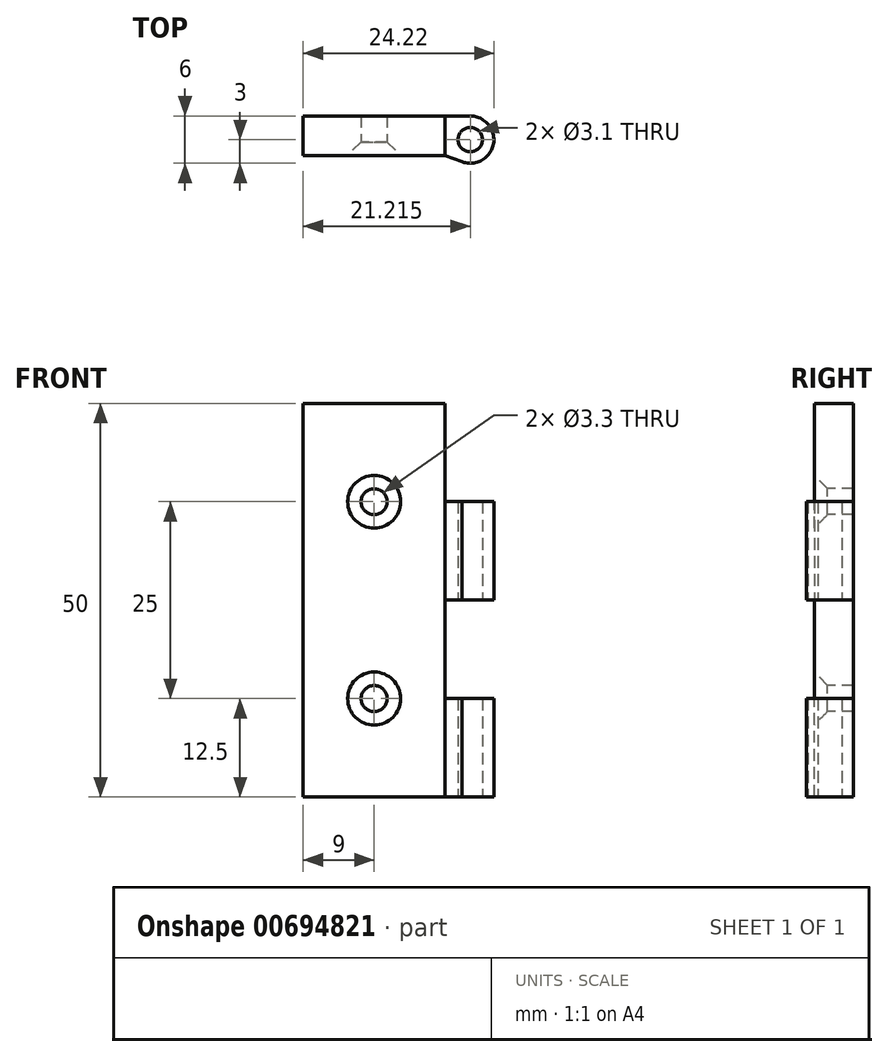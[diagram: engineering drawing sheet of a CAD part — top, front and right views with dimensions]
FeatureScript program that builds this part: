
annotation { "Feature Type Name" : "Feature", "Feature Type Description" : "" }
export const myFeature = defineFeature(function(context is Context, id is Id, definition is map)
    precondition{}
    {
        {
            var Q0;
            Q0=qCreatedBy(makeId("Front.planeOp"),FACE);
            var sketch = newSketch(context, id + "F0", { "sketchPlane" : qUnion([Q0])});
            skLineSegment(sketch, "E0.bottom", {"start": v(0, 0) * mm, "end": v(18, 0) * mm});
            skLineSegment(sketch, "E0.top", {"start": v(0, 50) * mm, "end": v(18, 50) * mm});
            skLineSegment(sketch, "E0.left", {"start": v(0, 0) * mm, "end": v(0, 50) * mm});
            skLineSegment(sketch, "E0.right", {"start": v(18, 0) * mm, "end": v(18, 50) * mm});
            skSolve(sketch);
        }
        {
            var Q0;
            Q0 = qSketchRegion(id + "F0", true);
            extrude(context, id + "F1", {"entities" : qUnion([Q0]), "depth" : 5 * mm, "offsetDistance" : 25 * mm});
        }
        {
            var Q0;
            Q0=makeQuery(id+"F1.opExtrude","SWEPT_FACE",FACE,{"disambiguationData":[OSD([sQuery(id+"F0.wireOp",EDGE,"E0.bottom")])]});
            var sketch = newSketch(context, id + "F2", { "sketchPlane" : qUnion([Q0])});
            skCircle(sketch, "E1", {"center": v(21.22, 3) * mm, "radius": 1.55 * mm});
            skArc(sketch, "E2", {"start": v(21.22, 0) * mm, "mid": v(24.17, 3.52) * mm, "end": v(20.2, 5.82) * mm});
            skLineSegment(sketch, "E3", {"start": v(21.22, 0) * mm, "end": v(18, 0) * mm});
            skLineSegment(sketch, "E4", {"start": v(18, 5) * mm, "end": v(20.2, 5.82) * mm});
            skSolve(sketch);
        }
        {
            var Q0;
            Q0=makeQuery(id+"F2.imprint","IMPRINT",FACE,{"disambiguationData":[TD([[makeQuery(id+"F2.imprint","IMPRINT",EDGE,{"derivedFrom":sQuery(id+"F2.wireOp",EDGE,"E1")}),-1.0]])]});
            extrude(context, id + "F3", {"entities" : qUnion([Q0]), "operationType" : NewBodyOperationType.ADD, "oppositeDirection" : true, "depth" : 12.5 * mm, "offsetDistance" : 25 * mm});
        }
        {
            var Q0;
            Q0=qCreatedBy(makeId("Top.planeOp"),FACE);
            cPlane(context, id + "F4", {"entities" : qUnion([Q0]), "cplaneType" : CPlaneType.OFFSET, "offset" : 25 * mm, "width" : 150 * mm, "height" : 150 * mm});
        }
        {
            var Q0;
            Q0=qCreatedBy(id+"F4.planeOp",FACE);
            var sketch = newSketch(context, id + "F5", { "sketchPlane" : qUnion([Q0])});
            skLineSegment(sketch, "E5.0", {"start": v(18, -5) * mm, "end": v(20.2, -5.82) * mm});
            skArc(sketch, "E6.0", {"start": v(21.22, 0) * mm, "mid": v(24.17, -3.52) * mm, "end": v(20.2, -5.82) * mm});
            skCircle(sketch, "E7.0", {"center": v(21.22, -3) * mm, "radius": 1.55 * mm});
            skLineSegment(sketch, "E8.0", {"start": v(21.22, 0) * mm, "end": v(18, 0) * mm});
            skLineSegment(sketch, "E9.0", {"start": v(18, -5) * mm, "end": v(18, 0) * mm});
            skSolve(sketch);
        }
        {
            var Q0;
            Q0=makeQuery(id+"F5.imprint","IMPRINT",FACE,{"disambiguationData":[TD([[makeQuery(id+"F5.imprint","IMPRINT",EDGE,{"derivedFrom":sQuery(id+"F5.wireOp",EDGE,"E5.0")}),1.0]])]});
            extrude(context, id + "F6", {"entities" : qUnion([Q0]), "operationType" : NewBodyOperationType.ADD, "depth" : 12.5 * mm, "offsetDistance" : 25 * mm});
        }
        {
            var Q0;
            Q0=makeQuery(id+"F1.opExtrude","CAP_FACE",FACE,{"disambiguationData":[OSD([sQuery(id+"F0.wireOp",EDGE,"E0.bottom"),sQuery(id+"F0.wireOp",EDGE,"E0.top"),sQuery(id+"F0.wireOp",EDGE,"E0.left"),sQuery(id+"F0.wireOp",EDGE,"E0.right")])],"isStart":false});
            var sketch = newSketch(context, id + "F7", { "sketchPlane" : qUnion([Q0])});
            skLineSegment(sketch, "E10", {"start": v(9, 0) * mm, "end": v(9, 50) * mm});
            skLineSegment(sketch, "E11", {"start": v(0, 25) * mm, "end": v(18, 25) * mm});
            skLineSegment(sketch, "E12", {"start": v(0, 25) * mm, "end": v(0, 50) * mm});
            skLineSegment(sketch, "E13", {"start": v(0, 25) * mm, "end": v(0, 0) * mm});
            skPoint(sketch, "E14", {"position": v(9, 12.5) * mm});
            skPoint(sketch, "E14.positionSnap0", {"position": v(0, 12.5) * mm});
            skPoint(sketch, "E15", {"position": v(9, 37.5) * mm});
            skPoint(sketch, "E15.positionSnap0", {"position": v(0, 37.5) * mm});
            skSolve(sketch);
        }
        {
            var Q0;
            Q0=sQuery(id+"F7.wireOp",VERTEX,"E15");
            var Q1;
            Q1=sQuery(id+"F7.wireOp",VERTEX,"E14");
            var Q2;
            Q2=makeQuery(id+"F1.opExtrude","SWEPT_BODY",BODY,{"disambiguationData":[OSD([sQuery(id+"F0.wireOp",EDGE,"E0.bottom"),sQuery(id+"F0.wireOp",EDGE,"E0.top"),sQuery(id+"F0.wireOp",EDGE,"E0.left"),sQuery(id+"F0.wireOp",EDGE,"E0.right")])]});
            hole(context, id + "F8", {"style" : HoleStyle.C_SINK, "endStyle" : HoleEndStyle.BLIND, "standardTappedOrClearance" : lookupTablePath({ "standard" : "ISO", "fit" : "Normal", "size" : "M3", "type" : "Clearance" }), "standardBlindInLast" : lookupTablePath({ "fit" : "Standard", "standard" : "ISO", "size" : "M3", "type" : "Clearance" }), "holeDiameter" : 3.3 * mm, "cSinkDiameter" : 6.72 * mm, "cSinkAngle" : 90 * degree, "majorDiameter" : 5 * mm, "holeDepth" : 40 * mm, "isTappedThrough" : true, "tappedDepth" : 12 * mm, "tapClearance" : 3, "locations" : qUnion([Q0, Q1]), "scope" : qUnion([Q2])});
        }
    });
